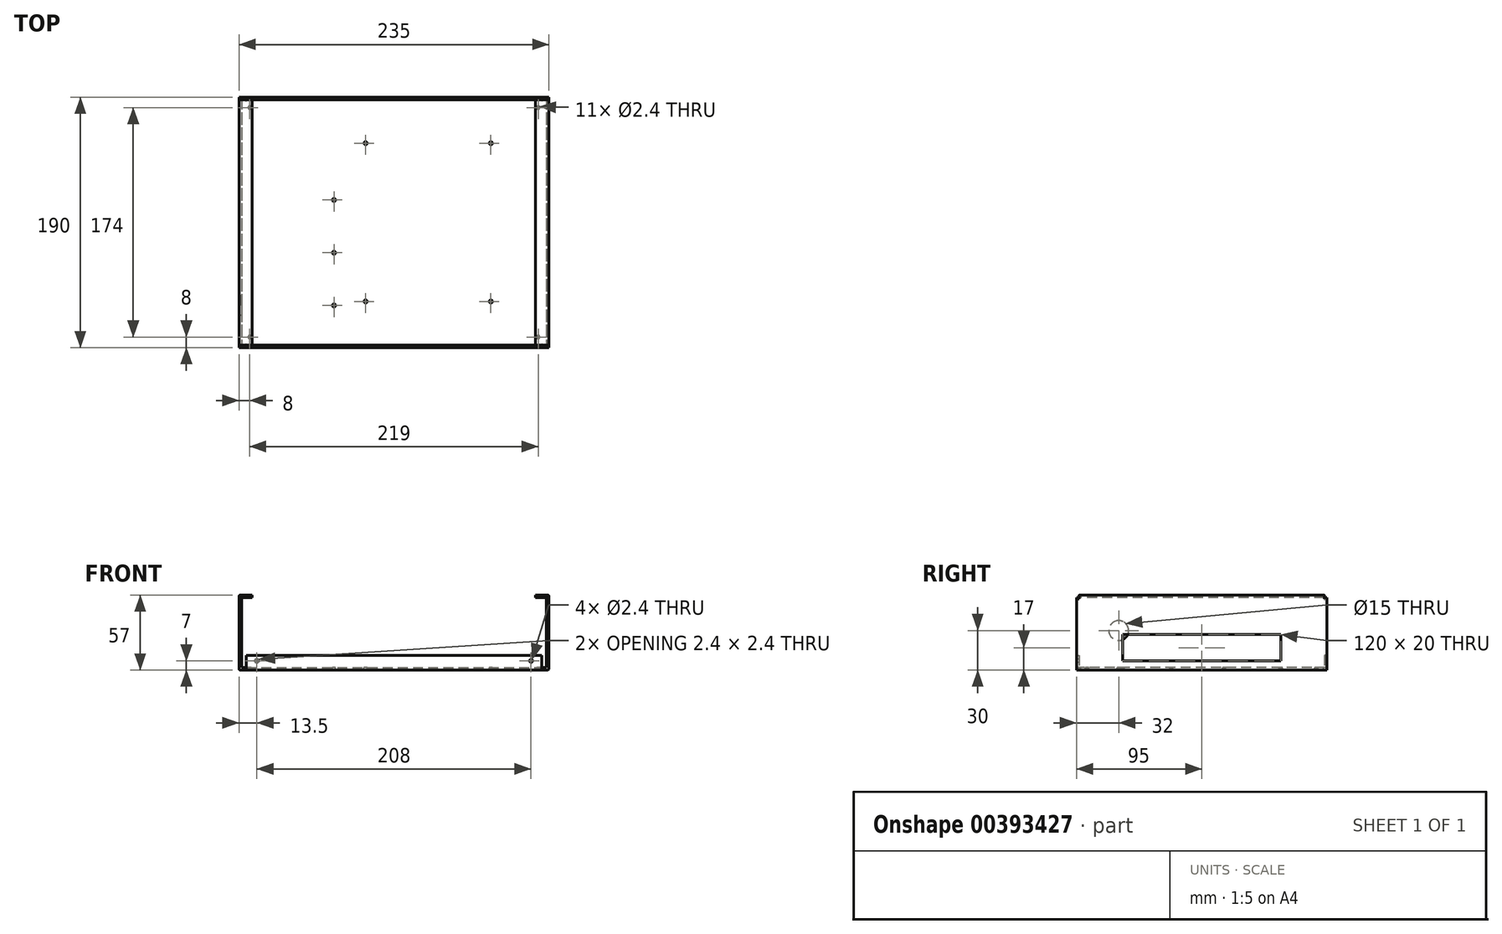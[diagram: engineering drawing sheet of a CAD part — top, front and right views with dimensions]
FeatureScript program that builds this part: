
annotation { "Feature Type Name" : "Feature", "Feature Type Description" : "" }
export const myFeature = defineFeature(function(context is Context, id is Id, definition is map)
    precondition{}
    {
        {
            var Q0;
            Q0=qCreatedBy(makeId("Top.planeOp"),FACE);
            var sketch = newSketch(context, id + "F0", { "sketchPlane" : qUnion([Q0])});
            skLineSegment(sketch, "E0.bottom", {"start": v(117.5, -95) * mm, "end": v(112.5, -95) * mm});
            skLineSegment(sketch, "E0.top", {"start": v(117.5, 95) * mm, "end": v(112.5, 95) * mm});
            skLineSegment(sketch, "E0.left", {"start": v(117.5, -95) * mm, "end": v(117.5, 95) * mm});
            skLineSegment(sketch, "E0.right", {"start": v(-117.5, -95) * mm, "end": v(-117.5, 95) * mm});
            skPoint(sketch, "E0.middle", {"position": v(0, 0) * mm});
            skLineSegment(sketch, "E1.top", {"start": v(-112.5, -92) * mm, "end": v(-112, -92) * mm});
            skLineSegment(sketch, "E1.left", {"start": v(-112.5, -95) * mm, "end": v(-112.5, -92) * mm});
            skLineSegment(sketch, "E1.right", {"start": v(-112, -95) * mm, "end": v(-112, -92) * mm});
            skLineSegment(sketch, "E2.trimOffspring", {"start": v(-112.5, -95) * mm, "end": v(-117.5, -95) * mm});
            skLineSegment(sketch, "E3.top", {"start": v(112, -92) * mm, "end": v(112.5, -92) * mm});
            skLineSegment(sketch, "E3.left", {"start": v(112, -95) * mm, "end": v(112, -92) * mm});
            skLineSegment(sketch, "E3.right", {"start": v(112.5, -95) * mm, "end": v(112.5, -92) * mm});
            skLineSegment(sketch, "E4.trimOffspring", {"start": v(112, -95) * mm, "end": v(-112, -95) * mm});
            skLineSegment(sketch, "E5.top", {"start": v(-112.5, 92) * mm, "end": v(-112, 92) * mm});
            skLineSegment(sketch, "E5.left", {"start": v(-112.5, 95) * mm, "end": v(-112.5, 92) * mm});
            skLineSegment(sketch, "E5.right", {"start": v(-112, 95) * mm, "end": v(-112, 92) * mm});
            skLineSegment(sketch, "E6.top", {"start": v(112.5, 92) * mm, "end": v(112, 92) * mm});
            skLineSegment(sketch, "E6.left", {"start": v(112.5, 95) * mm, "end": v(112.5, 92) * mm});
            skLineSegment(sketch, "E6.right", {"start": v(112, 95) * mm, "end": v(112, 92) * mm});
            skLineSegment(sketch, "E7.trimOffspring", {"start": v(-112.5, 95) * mm, "end": v(-117.5, 95) * mm});
            skLineSegment(sketch, "E8.trimOffspring", {"start": v(112, 95) * mm, "end": v(-112, 95) * mm});
            skSolve(sketch);
        }
        {
            var Q0;
            Q0=qSketchRegion(id+"F0",true);
            extrude(context, id + "F1", {"entities" : qUnion([Q0]), "depth" : 2 * mm});
        }
        {
            var Q0;
            Q0=makeQuery(id+"F1.opExtrude","CAP_FACE",FACE,{"disambiguationData":[OSD([sQuery(id+"F0.wireOp",EDGE,"E0.bottom"),sQuery(id+"F0.wireOp",EDGE,"E0.top"),sQuery(id+"F0.wireOp",EDGE,"E0.left"),sQuery(id+"F0.wireOp",EDGE,"E0.right")])],"isStart":false});
            var sketch = newSketch(context, id + "F2", { "sketchPlane" : qUnion([Q0])});
            skLineSegment(sketch, "E9.bottom", {"start": v(117.5, 95) * mm, "end": v(115.5, 95) * mm});
            skLineSegment(sketch, "E9.top", {"start": v(117.5, -95) * mm, "end": v(115.5, -95) * mm});
            skLineSegment(sketch, "E9.left", {"start": v(117.5, 95) * mm, "end": v(117.5, -95) * mm});
            skLineSegment(sketch, "E9.right", {"start": v(115.5, 95) * mm, "end": v(115.5, -95) * mm});
            skLineSegment(sketch, "E10.bottom", {"start": v(-117.5, 95) * mm, "end": v(-115.5, 95) * mm});
            skLineSegment(sketch, "E10.top", {"start": v(-117.5, -95) * mm, "end": v(-115.5, -95) * mm});
            skLineSegment(sketch, "E10.left", {"start": v(-117.5, 95) * mm, "end": v(-117.5, -95) * mm});
            skLineSegment(sketch, "E10.right", {"start": v(-115.5, 95) * mm, "end": v(-115.5, -95) * mm});
            skSolve(sketch);
        }
        {
            var Q0;
            Q0=qSketchRegion(id+"F2",true);
            extrude(context, id + "F3", {"entities" : qUnion([Q0]), "operationType" : NewBodyOperationType.ADD, "depth" : 53 * mm});
        }
        {
            var Q0;
            Q0=makeQuery(id+"F1.opExtrude","CAP_EDGE",EDGE,{"disambiguationData":[OSD([sQuery(id+"F0.wireOp",EDGE,"E0.right")])],"isStart":true});
            var Q1;
            Q1=makeQuery(id+"F1.opExtrude","CAP_EDGE",EDGE,{"disambiguationData":[OSD([sQuery(id+"F0.wireOp",EDGE,"E0.left")])],"isStart":true});
            var Q2;
            Q2=makeQuery(id+"F3.opExtrude","CAP_EDGE",EDGE,{"disambiguationData":[OSD([sQuery(id+"F2.wireOp",EDGE,"E10.right")])],"isStart":true});
            var Q3;
            Q3=makeQuery(id+"F3.opExtrude","CAP_EDGE",EDGE,{"disambiguationData":[OSD([sQuery(id+"F2.wireOp",EDGE,"E9.right")])],"isStart":true});
            fillet(context, id + "F4", {"entities" : qUnion([Q0, Q1, Q2, Q3]), "radius" : 1 * mm, "tangentPropagation" : true, "allowEdgeOverflow" : false});
        }
        {
            var Q0;
            Q0=makeQuery(id+"F3.opExtrude","CAP_FACE",FACE,{"disambiguationData":[OSD([sQuery(id+"F2.wireOp",EDGE,"E10.bottom"),sQuery(id+"F2.wireOp",EDGE,"E10.top"),sQuery(id+"F2.wireOp",EDGE,"E10.left"),sQuery(id+"F2.wireOp",EDGE,"E10.right")])],"isStart":false});
            var sketch = newSketch(context, id + "F5", { "sketchPlane" : qUnion([Q0])});
            skLineSegment(sketch, "E11.bottom", {"start": v(-117.5, 93) * mm, "end": v(-107.5, 93) * mm});
            skLineSegment(sketch, "E11.top", {"start": v(-117.5, -93) * mm, "end": v(-107.5, -93) * mm});
            skLineSegment(sketch, "E11.left", {"start": v(-117.5, 93) * mm, "end": v(-117.5, -93) * mm});
            skLineSegment(sketch, "E11.right", {"start": v(-107.5, 93) * mm, "end": v(-107.5, -93) * mm});
            skLineSegment(sketch, "E12.bottom", {"start": v(107.5, 93) * mm, "end": v(117.5, 93) * mm});
            skLineSegment(sketch, "E12.top", {"start": v(107.5, -93) * mm, "end": v(117.5, -93) * mm});
            skLineSegment(sketch, "E12.left", {"start": v(107.5, 93) * mm, "end": v(107.5, -93) * mm});
            skLineSegment(sketch, "E12.right", {"start": v(117.5, 93) * mm, "end": v(117.5, -93) * mm});
            skSolve(sketch);
        }
        {
            var Q0;
            Q0=qSketchRegion(id+"F5",true);
            extrude(context, id + "F6", {"entities" : qUnion([Q0]), "operationType" : NewBodyOperationType.ADD, "depth" : 2 * mm});
        }
        {
            var Q0;
            Q0=makeQuery(id+"F6.opExtrude","CAP_EDGE",EDGE,{"disambiguationData":[OSD([sQuery(id+"F5.wireOp",EDGE,"E11.left")])],"isStart":false});
            var Q1;
            Q1=makeQuery(id+"F6.opExtrude","CAP_EDGE",EDGE,{"disambiguationData":[OSD([sQuery(id+"F5.wireOp",EDGE,"E12.right")])],"isStart":false});
            var Q2;
            {var subQ0=sQuery(id+"F5.wireOp",EDGE,"E11.top");var subQ1=sQuery(id+"F5.wireOp",EDGE,"E11.bottom");var subQ2=sQuery(id+"F2.wireOp",EDGE,"E10.right");Q2=makeQuery(id+"F6.boolean.opBoolean","SPLIT",EDGE,{"disambiguationData":[TD([makeQuery(id+"F3.opExtrude","CAP_FACE",FACE,{"disambiguationData":[OSD([sQuery(id+"F2.wireOp",EDGE,"E10.bottom"),sQuery(id+"F2.wireOp",EDGE,"E10.top"),sQuery(id+"F2.wireOp",EDGE,"E10.left"),subQ2])],"isStart":false}),makeQuery(id+"F3.opExtrude","SWEPT_FACE",FACE,{"disambiguationData":[OSD([subQ2])]}),makeQuery(id+"F6.opExtrude","SWEPT_FACE",FACE,{"disambiguationData":[OSD([subQ1])]}),makeQuery(id+"F6.opExtrude","CAP_FACE",FACE,{"disambiguationData":[OSD([subQ1,subQ0,sQuery(id+"F5.wireOp",EDGE,"E11.left"),sQuery(id+"F5.wireOp",EDGE,"E11.right")])],"isStart":true}),makeQuery(id+"F6.opExtrude","SWEPT_FACE",FACE,{"disambiguationData":[OSD([subQ0])]})])],"derivedFrom":makeQuery(id+"F3.opExtrude","CAP_EDGE",EDGE,{"disambiguationData":[OSD([subQ2])],"isStart":false})});}
            var Q3;
            {var subQ0=sQuery(id+"F5.wireOp",EDGE,"E12.top");var subQ1=sQuery(id+"F5.wireOp",EDGE,"E12.bottom");var subQ2=sQuery(id+"F2.wireOp",EDGE,"E9.right");Q3=makeQuery(id+"F6.boolean.opBoolean","SPLIT",EDGE,{"disambiguationData":[TD([makeQuery(id+"F3.opExtrude","CAP_FACE",FACE,{"disambiguationData":[OSD([sQuery(id+"F2.wireOp",EDGE,"E9.bottom"),sQuery(id+"F2.wireOp",EDGE,"E9.top"),sQuery(id+"F2.wireOp",EDGE,"E9.left"),subQ2])],"isStart":false}),makeQuery(id+"F3.opExtrude","SWEPT_FACE",FACE,{"disambiguationData":[OSD([subQ2])]}),makeQuery(id+"F6.opExtrude","SWEPT_FACE",FACE,{"disambiguationData":[OSD([subQ1])]}),makeQuery(id+"F6.opExtrude","CAP_FACE",FACE,{"disambiguationData":[OSD([subQ1,subQ0,sQuery(id+"F5.wireOp",EDGE,"E12.left"),sQuery(id+"F5.wireOp",EDGE,"E12.right")])],"isStart":true}),makeQuery(id+"F6.opExtrude","SWEPT_FACE",FACE,{"disambiguationData":[OSD([subQ0])]})])],"derivedFrom":makeQuery(id+"F3.opExtrude","CAP_EDGE",EDGE,{"disambiguationData":[OSD([subQ2])],"isStart":false})});}
            fillet(context, id + "F7", {"entities" : qUnion([Q0, Q1, Q2, Q3]), "radius" : 1 * mm, "tangentPropagation" : true, "allowEdgeOverflow" : false});
        }
        {
            var Q0;
            Q0=makeQuery(id+"F1.opExtrude","CAP_FACE",FACE,{"disambiguationData":[OSD([sQuery(id+"F0.wireOp",EDGE,"E0.bottom"),sQuery(id+"F0.wireOp",EDGE,"E0.top"),sQuery(id+"F0.wireOp",EDGE,"E0.left"),sQuery(id+"F0.wireOp",EDGE,"E0.right"),sQuery(id+"F0.wireOp",EDGE,"E1.top"),sQuery(id+"F0.wireOp",EDGE,"E1.left"),sQuery(id+"F0.wireOp",EDGE,"E1.right"),sQuery(id+"F0.wireOp",EDGE,"E2.trimOffspring"),sQuery(id+"F0.wireOp",EDGE,"E3.top"),sQuery(id+"F0.wireOp",EDGE,"E3.left"),sQuery(id+"F0.wireOp",EDGE,"E3.right"),sQuery(id+"F0.wireOp",EDGE,"E4.trimOffspring")])],"isStart":false});
            var sketch = newSketch(context, id + "F8", { "sketchPlane" : qUnion([Q0])});
            skLineSegment(sketch, "E13.bottom", {"start": v(-112, -93) * mm, "end": v(112, -93) * mm});
            skLineSegment(sketch, "E13.top", {"start": v(-112, -95) * mm, "end": v(112, -95) * mm});
            skLineSegment(sketch, "E13.left", {"start": v(-112, -93) * mm, "end": v(-112, -95) * mm});
            skLineSegment(sketch, "E13.right", {"start": v(112, -93) * mm, "end": v(112, -95) * mm});
            skLineSegment(sketch, "E14.bottom", {"start": v(-112, 95) * mm, "end": v(112, 95) * mm});
            skLineSegment(sketch, "E14.top", {"start": v(-112, 93) * mm, "end": v(112, 93) * mm});
            skLineSegment(sketch, "E14.left", {"start": v(-112, 95) * mm, "end": v(-112, 93) * mm});
            skLineSegment(sketch, "E14.right", {"start": v(112, 95) * mm, "end": v(112, 93) * mm});
            skSolve(sketch);
        }
        {
            var Q0;
            Q0=qSketchRegion(id+"F8",true);
            extrude(context, id + "F9", {"entities" : qUnion([Q0]), "operationType" : NewBodyOperationType.ADD, "depth" : 9 * mm});
        }
        {
            var Q0;
            Q0=makeQuery(id+"F1.opExtrude","CAP_EDGE",EDGE,{"disambiguationData":[OSD([sQuery(id+"F0.wireOp",EDGE,"E4.trimOffspring")])],"isStart":true});
            var Q1;
            Q1=makeQuery(id+"F9.opExtrude","CAP_EDGE",EDGE,{"disambiguationData":[OSD([sQuery(id+"F8.wireOp",EDGE,"E13.bottom")])],"isStart":true});
            var Q2;
            Q2=makeQuery(id+"F9.opExtrude","CAP_EDGE",EDGE,{"disambiguationData":[OSD([sQuery(id+"F8.wireOp",EDGE,"E14.top")])],"isStart":true});
            var Q3;
            Q3=makeQuery(id+"F1.opExtrude","CAP_EDGE",EDGE,{"disambiguationData":[OSD([sQuery(id+"F0.wireOp",EDGE,"E8.trimOffspring")])],"isStart":true});
            fillet(context, id + "F10", {"entities" : qUnion([Q0, Q1, Q2, Q3]), "radius" : 1 * mm, "tangentPropagation" : true, "allowEdgeOverflow" : false});
        }
        {
            var Q0;
            Q0=makeQuery(id+"F6.boolean.opBoolean","MERGE",FACE,{"derivedFrom":[makeQuery(id+"F3.boolean.opBoolean","MERGE",FACE,{"derivedFrom":[makeQuery(id+"F1.opExtrude","SWEPT_FACE",FACE,{"disambiguationData":[OSD([sQuery(id+"F0.wireOp",EDGE,"E0.right")])]}),makeQuery(id+"F3.opExtrude","SWEPT_FACE",FACE,{"disambiguationData":[OSD([sQuery(id+"F2.wireOp",EDGE,"LtGDmYED-3yVl-KpR6-pZyB-YukeFVbaKuZ8.left")])]})]}),makeQuery(id+"F6.opExtrude","SWEPT_FACE",FACE,{"disambiguationData":[OSD([sQuery(id+"F5.wireOp",EDGE,"E11.left")])]})]});
            var sketch = newSketch(context, id + "F11", { "sketchPlane" : qUnion([Q0])});
            skLineSegment(sketch, "E15.bottom", {"start": v(93, 55) * mm, "end": v(93.5, 55) * mm});
            skLineSegment(sketch, "E15.top", {"start": v(93, 54) * mm, "end": v(93.5, 54) * mm});
            skLineSegment(sketch, "E15.left", {"start": v(93, 55) * mm, "end": v(93, 54) * mm});
            skLineSegment(sketch, "E15.right", {"start": v(93.5, 55) * mm, "end": v(93.5, 54) * mm});
            skLineSegment(sketch, "E16.bottom", {"start": v(-93, 55) * mm, "end": v(-93.5, 55) * mm});
            skLineSegment(sketch, "E16.top", {"start": v(-93, 54) * mm, "end": v(-93.5, 54) * mm});
            skLineSegment(sketch, "E16.left", {"start": v(-93, 55) * mm, "end": v(-93, 54) * mm});
            skLineSegment(sketch, "E16.right", {"start": v(-93.5, 55) * mm, "end": v(-93.5, 54) * mm});
            skSolve(sketch);
        }
        {
            var Q0;
            Q0=qSketchRegion(id+"F11",true);
            extrude(context, id + "F12", {"entities" : qUnion([Q0]), "operationType" : NewBodyOperationType.REMOVE, "endBound" : BoundingType.THROUGH_ALL, "oppositeDirection" : true, "depth" : 25 * mm});
        }
        {
            var Q0;
            Q0=makeQuery(id+"F6.boolean.opBoolean","MERGE",FACE,{"derivedFrom":[makeQuery(id+"F3.boolean.opBoolean","MERGE",FACE,{"derivedFrom":[makeQuery(id+"F1.opExtrude","SWEPT_FACE",FACE,{"disambiguationData":[OSD([sQuery(id+"F0.wireOp",EDGE,"E0.right")])]}),makeQuery(id+"F3.opExtrude","SWEPT_FACE",FACE,{"disambiguationData":[OSD([sQuery(id+"F2.wireOp",EDGE,"E10.left")])]})]}),makeQuery(id+"F6.opExtrude","SWEPT_FACE",FACE,{"disambiguationData":[OSD([sQuery(id+"F5.wireOp",EDGE,"E11.left")])]})]});
            var sketch = newSketch(context, id + "F13", { "sketchPlane" : qUnion([Q0])});
            skCircle(sketch, "E17", {"center": v(63, 30) * mm, "radius": 7.5 * mm});
            skSolve(sketch);
        }
        {
            var Q0;
            Q0=qSketchRegion(id+"F13",true);
            extrude(context, id + "F14", {"entities" : qUnion([Q0]), "operationType" : NewBodyOperationType.REMOVE, "oppositeDirection" : true, "depth" : 3 * mm});
        }
        {
            var Q0;
            Q0=makeQuery(id+"F1.opExtrude","CAP_FACE",FACE,{"disambiguationData":[OSD([sQuery(id+"F0.wireOp",EDGE,"E0.bottom"),sQuery(id+"F0.wireOp",EDGE,"E0.top"),sQuery(id+"F0.wireOp",EDGE,"E0.left"),sQuery(id+"F0.wireOp",EDGE,"E0.right"),sQuery(id+"F0.wireOp",EDGE,"E1.top"),sQuery(id+"F0.wireOp",EDGE,"E1.left"),sQuery(id+"F0.wireOp",EDGE,"E1.right"),sQuery(id+"F0.wireOp",EDGE,"E2.trimOffspring"),sQuery(id+"F0.wireOp",EDGE,"E3.top"),sQuery(id+"F0.wireOp",EDGE,"E3.left"),sQuery(id+"F0.wireOp",EDGE,"E3.right"),sQuery(id+"F0.wireOp",EDGE,"E4.trimOffspring"),sQuery(id+"F0.wireOp",EDGE,"E5.top"),sQuery(id+"F0.wireOp",EDGE,"E5.left"),sQuery(id+"F0.wireOp",EDGE,"E5.right"),sQuery(id+"F0.wireOp",EDGE,"E6.top"),sQuery(id+"F0.wireOp",EDGE,"E6.left"),sQuery(id+"F0.wireOp",EDGE,"E6.right"),sQuery(id+"F0.wireOp",EDGE,"E7.trimOffspring"),sQuery(id+"F0.wireOp",EDGE,"E8.trimOffspring")])],"isStart":false});
            var sketch = newSketch(context, id + "F15", { "sketchPlane" : qUnion([Q0])});
            skCircle(sketch, "E18", {"center": v(-109.5, 87) * mm, "radius": 1.2 * mm});
            skCircle(sketch, "E19", {"center": v(109.5, 87) * mm, "radius": 1.2 * mm});
            skCircle(sketch, "E20", {"center": v(-109.5, -87) * mm, "radius": 1.2 * mm});
            skCircle(sketch, "E21", {"center": v(109.5, -87) * mm, "radius": 1.2 * mm});
            skCircle(sketch, "E22", {"center": v(-21.5, 60) * mm, "radius": 1.2 * mm});
            skCircle(sketch, "E23", {"center": v(73.5, 60) * mm, "radius": 1.2 * mm});
            skCircle(sketch, "E24", {"center": v(-21.5, -60) * mm, "radius": 1.2 * mm});
            skCircle(sketch, "E25", {"center": v(73.5, -60) * mm, "radius": 1.2 * mm});
            skLineSegment(sketch, "E26.bottom", {"start": v(113.5, -75) * mm, "end": v(-36.5, -75) * mm, "construction": true});
            skLineSegment(sketch, "E26.top", {"start": v(113.5, 75) * mm, "end": v(-36.5, 75) * mm, "construction": true});
            skLineSegment(sketch, "E26.left", {"start": v(113.5, -75) * mm, "end": v(113.5, 75) * mm, "construction": true});
            skLineSegment(sketch, "E26.right", {"start": v(-36.5, -75) * mm, "end": v(-36.5, 75) * mm, "construction": true});
            skPoint(sketch, "E26.middle", {"position": v(38.5, 0) * mm});
            skCircle(sketch, "E27", {"center": v(-45.5, 17) * mm, "radius": 1.2 * mm});
            skCircle(sketch, "E28", {"center": v(-45.5, -23) * mm, "radius": 1.2 * mm});
            skCircle(sketch, "E29", {"center": v(-45.5, -63) * mm, "radius": 1.2 * mm});
            skLineSegment(sketch, "E30.bottom", {"start": v(-38.5, -83) * mm, "end": v(-49.5, -83) * mm, "construction": true});
            skLineSegment(sketch, "E30.top", {"start": v(-38.5, 37) * mm, "end": v(-49.5, 37) * mm, "construction": true});
            skLineSegment(sketch, "E30.left", {"start": v(-38.5, -83) * mm, "end": v(-38.5, 37) * mm, "construction": true});
            skLineSegment(sketch, "E30.right", {"start": v(-49.5, -83) * mm, "end": v(-49.5, 37) * mm, "construction": true});
            skPoint(sketch, "E30.middle", {"position": v(-44, -23) * mm});
            skSolve(sketch);
        }
        {
            var Q0;
            Q0=qSketchRegion(id+"F15",true);
            extrude(context, id + "F16", {"entities" : qUnion([Q0]), "operationType" : NewBodyOperationType.REMOVE, "oppositeDirection" : true, "depth" : 3 * mm});
        }
        {
            var Q0;
            Q0=makeQuery(id+"F9.boolean.opBoolean","MERGE",FACE,{"derivedFrom":[makeQuery(id+"F1.opExtrude","SWEPT_FACE",FACE,{"disambiguationData":[OSD([sQuery(id+"F0.wireOp",EDGE,"E4.trimOffspring")])]}),makeQuery(id+"F9.opExtrude","SWEPT_FACE",FACE,{"disambiguationData":[OSD([sQuery(id+"F8.wireOp",EDGE,"E13.top")])]})]});
            var sketch = newSketch(context, id + "F17", { "sketchPlane" : qUnion([Q0])});
            skCircle(sketch, "E31", {"center": v(104, 7) * mm, "radius": 1.2 * mm});
            skCircle(sketch, "E32", {"center": v(-104, 7) * mm, "radius": 1.2 * mm});
            skSolve(sketch);
        }
        {
            var Q0;
            Q0=qSketchRegion(id+"F17",true);
            extrude(context, id + "F18", {"entities" : qUnion([Q0]), "operationType" : NewBodyOperationType.REMOVE, "endBound" : BoundingType.THROUGH_ALL, "oppositeDirection" : true, "depth" : 25 * mm});
        }
        {
            var Q0;
            Q0=makeQuery(id+"F6.boolean.opBoolean","MERGE",FACE,{"derivedFrom":[makeQuery(id+"F3.boolean.opBoolean","MERGE",FACE,{"derivedFrom":[makeQuery(id+"F1.opExtrude","SWEPT_FACE",FACE,{"disambiguationData":[OSD([sQuery(id+"F0.wireOp",EDGE,"E0.left")])]}),makeQuery(id+"F3.opExtrude","SWEPT_FACE",FACE,{"disambiguationData":[OSD([sQuery(id+"F2.wireOp",EDGE,"E9.left")])]})]}),makeQuery(id+"F6.opExtrude","SWEPT_FACE",FACE,{"disambiguationData":[OSD([sQuery(id+"F5.wireOp",EDGE,"E12.right")])]})]});
            var sketch = newSketch(context, id + "F19", { "sketchPlane" : qUnion([Q0])});
            skLineSegment(sketch, "E33.bottom", {"start": v(60, 7) * mm, "end": v(-60, 7) * mm});
            skLineSegment(sketch, "E33.top", {"start": v(60, 27) * mm, "end": v(-60, 27) * mm});
            skLineSegment(sketch, "E33.left", {"start": v(60, 7) * mm, "end": v(60, 27) * mm});
            skLineSegment(sketch, "E33.right", {"start": v(-60, 7) * mm, "end": v(-60, 27) * mm});
            skPoint(sketch, "E33.middle", {"position": v(0, 17) * mm});
            skSolve(sketch);
        }
        {
            var Q0;
            Q0=qSketchRegion(id+"F19",true);
            extrude(context, id + "F20", {"entities" : qUnion([Q0]), "operationType" : NewBodyOperationType.REMOVE, "oppositeDirection" : true, "depth" : 3 * mm});
        }
    });
